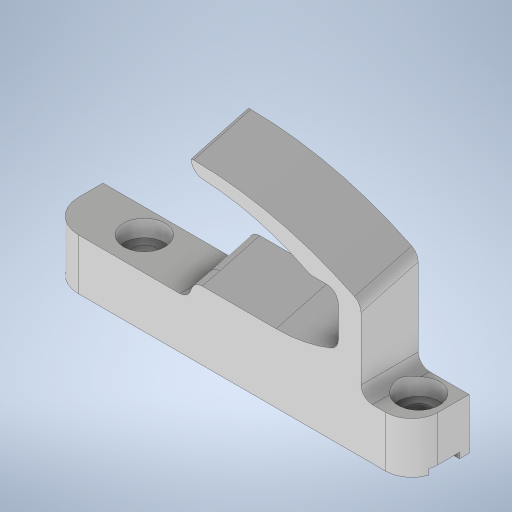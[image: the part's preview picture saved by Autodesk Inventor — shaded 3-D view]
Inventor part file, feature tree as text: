
AUTODESK INVENTOR PART (.ipt)
format: ipt  version: 2024 (Build 280153000, 153)  size: 375,808 bytes
history: native  units: mm
features: extrude x8, sketch x6, projected_geometry x2, plane x1, fillet x1
ambient origin geometry x8: Origin, YZ Plane, XZ Plane, XY Plane, X Axis, Y Axis, Z Axis, Center Point
bodies: Solid1 (feature_tree)
feature tree (18):
  sketch  "Sketch6"  dims[d31=30.0mm d32=0.0mm d33=11.0mm]
  plane  "Work Plane2"
  extrude  "Extrusion7"  TaperAngle=15.0deg  [1 undecoded]
  extrude  "Extrusion8"  Depth=11.0mm
  extrude  "Extrusion9"  Depth=5.0mm
  sketch  "Sketch10"  dims[d44=2.0mm d45=1.5mm d46=0.0mm]
  extrude  "Extrusion10"  Depth=2.0mm
  extrude  "Extrusion11"  Depth=10.0mm TaperAngle=0.0deg
  fillet  "Fillet1"  Radius=10.0mm
  sketch  "Sketch7"  dims[d34=10.9mm d35=0.0mm d36=5.0mm]
  sketch  "Sketch8"  dims[d37=2.0mm d38=5.0mm]
  sketch  "Sketch9"  dims[d39=2.4mm d40=10.9mm d41=0.0mm d42=10.0mm d43=0.0mm]
  projected_geometry  "Projected Loop3"
  projected_geometry  "Projected Loop4"
  sketch  "Sketch1"  dims[d0=10.0mm d1=3.2mm d2=1.0mm d3=3.0mm d4=7.3mm d5=3.2mm d6=4.1mm d7=48.5mm d9=0.0mm d10=1.0mm d12=0.0mm d13=8.0mm d15=0.0mm d16=5.0mm d30=15.0deg]
  extrude  "Extrusion1"  Depth=2.0mm TaperAngle=0.0deg
  extrude  "Extrusion2"  [1 undecoded]
  extrude  "Extrusion3"  [1 undecoded]
note: 3 required parameter values undecoded (feature->parameter linkage not recoverable at this tier; creation-order binding heuristic only, values carry confidence <= 0.55)
